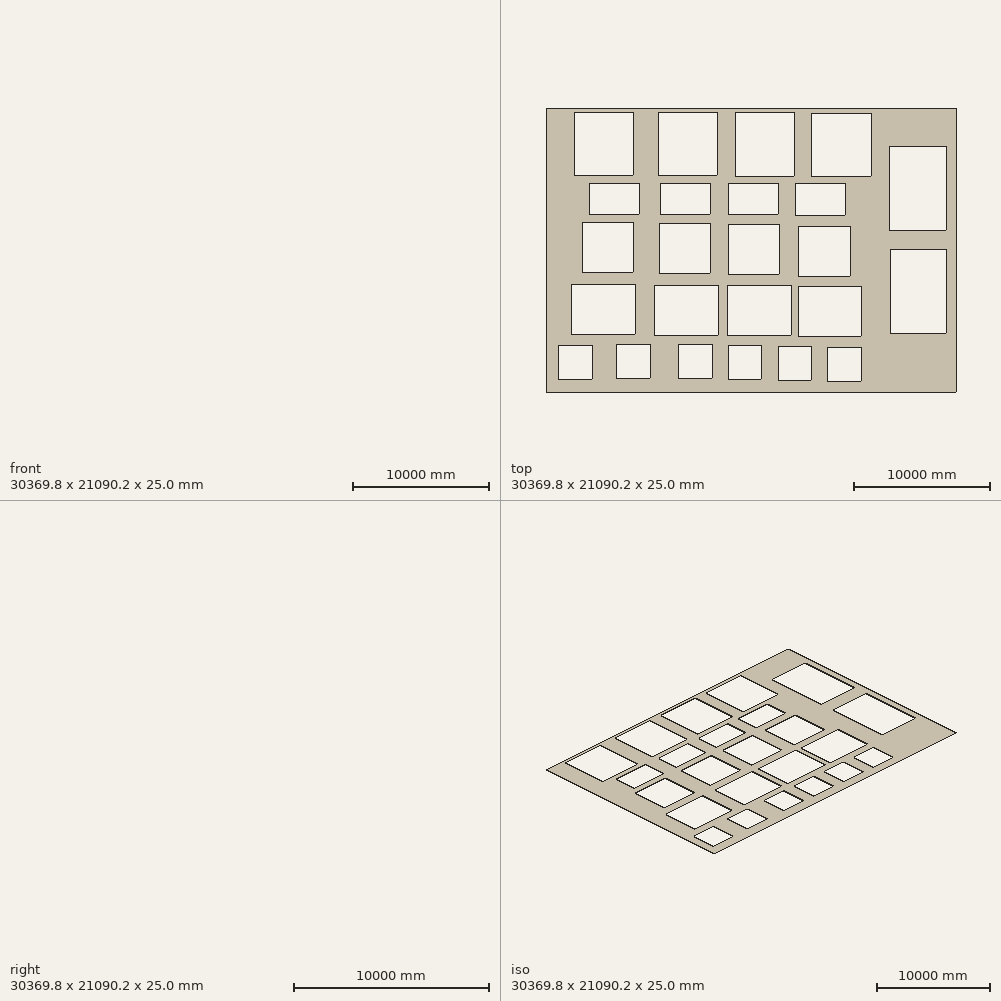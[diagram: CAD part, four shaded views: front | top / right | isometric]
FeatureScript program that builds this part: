
annotation { "Feature Type Name" : "Feature", "Feature Type Description" : "" }
export const myFeature = defineFeature(function(context is Context, id is Id, definition is map)
    precondition{}
    {
        {
            var Q0;
            Q0=qCreatedBy(makeId("Top.planeOp"),FACE);
            var sketch = newSketch(context, id + "F0", { "sketchPlane" : qUnion([Q0])});
            skLineSegment(sketch, "E0.bottom", {"start": v(-362.28, 2339.56) * mm, "end": v(3337.72, 2339.56) * mm});
            skLineSegment(sketch, "E0.top", {"start": v(-362.28, 39.56) * mm, "end": v(3337.72, 39.56) * mm});
            skLineSegment(sketch, "E0.left", {"start": v(-362.28, 2339.56) * mm, "end": v(-362.28, 39.56) * mm});
            skLineSegment(sketch, "E0.right", {"start": v(3337.72, 2339.56) * mm, "end": v(3337.72, 39.56) * mm});
            skLineSegment(sketch, "E1.bottom", {"start": v(-5538.63, 7611.88) * mm, "end": v(-1138.63, 7611.88) * mm});
            skLineSegment(sketch, "E1.top", {"start": v(-5538.63, 2911.88) * mm, "end": v(-1138.63, 2911.88) * mm});
            skLineSegment(sketch, "E1.left", {"start": v(-5538.63, 7611.88) * mm, "end": v(-5538.63, 2911.88) * mm});
            skLineSegment(sketch, "E1.right", {"start": v(-1138.63, 7611.88) * mm, "end": v(-1138.63, 2911.88) * mm});
            skLineSegment(sketch, "E2.bottom", {"start": v(4609.45, 2304.21) * mm, "end": v(8309.45, 2304.21) * mm});
            skLineSegment(sketch, "E2.top", {"start": v(4609.45, 4.21) * mm, "end": v(8309.45, 4.21) * mm});
            skLineSegment(sketch, "E2.left", {"start": v(4609.45, 2304.21) * mm, "end": v(4609.45, 4.21) * mm});
            skLineSegment(sketch, "E2.right", {"start": v(8309.45, 2304.21) * mm, "end": v(8309.45, 4.21) * mm});
            skLineSegment(sketch, "E3.bottom", {"start": v(-10619.1, 2366.7) * mm, "end": v(-6919.1, 2366.7) * mm});
            skLineSegment(sketch, "E3.top", {"start": v(-10619.1, 66.7) * mm, "end": v(-6919.1, 66.7) * mm});
            skLineSegment(sketch, "E3.left", {"start": v(-10619.1, 2366.7) * mm, "end": v(-10619.1, 66.7) * mm});
            skLineSegment(sketch, "E3.right", {"start": v(-6919.1, 2366.7) * mm, "end": v(-6919.1, 66.7) * mm});
            skLineSegment(sketch, "E4.bottom", {"start": v(-11738.1, 7598.85) * mm, "end": v(-7338.1, 7598.85) * mm});
            skLineSegment(sketch, "E4.top", {"start": v(-11738.1, 2898.85) * mm, "end": v(-7338.1, 2898.85) * mm});
            skLineSegment(sketch, "E4.left", {"start": v(-11738.1, 7598.85) * mm, "end": v(-11738.1, 2898.85) * mm});
            skLineSegment(sketch, "E4.right", {"start": v(-7338.1, 7598.85) * mm, "end": v(-7338.1, 2898.85) * mm});
            skLineSegment(sketch, "E5.bottom", {"start": v(-5346.09, 2331.36) * mm, "end": v(-1646.09, 2331.36) * mm});
            skLineSegment(sketch, "E5.top", {"start": v(-5346.09, 31.36) * mm, "end": v(-1646.09, 31.36) * mm});
            skLineSegment(sketch, "E5.left", {"start": v(-5346.09, 2331.36) * mm, "end": v(-5346.09, 31.36) * mm});
            skLineSegment(sketch, "E5.right", {"start": v(-1646.09, 2331.36) * mm, "end": v(-1646.09, 31.36) * mm});
            skLineSegment(sketch, "E6.bottom", {"start": v(156.32, 7588.05) * mm, "end": v(4556.32, 7588.05) * mm});
            skLineSegment(sketch, "E6.top", {"start": v(156.32, 2888.05) * mm, "end": v(4556.32, 2888.05) * mm});
            skLineSegment(sketch, "E6.left", {"start": v(156.32, 7588.05) * mm, "end": v(156.32, 2888.05) * mm});
            skLineSegment(sketch, "E6.right", {"start": v(4556.32, 7588.05) * mm, "end": v(4556.32, 2888.05) * mm});
            skLineSegment(sketch, "E7.bottom", {"start": v(-11167.32, -569.05) * mm, "end": v(-7367.32, -569.05) * mm});
            skLineSegment(sketch, "E7.top", {"start": v(-11167.32, -4269.05) * mm, "end": v(-7367.32, -4269.05) * mm});
            skLineSegment(sketch, "E7.left", {"start": v(-11167.32, -569.05) * mm, "end": v(-11167.32, -4269.05) * mm});
            skLineSegment(sketch, "E7.right", {"start": v(-7367.32, -569.05) * mm, "end": v(-7367.32, -4269.05) * mm});
            skLineSegment(sketch, "E8.bottom", {"start": v(-5464.05, -630.23) * mm, "end": v(-1664.05, -630.23) * mm});
            skLineSegment(sketch, "E8.top", {"start": v(-5464.05, -4330.23) * mm, "end": v(-1664.05, -4330.23) * mm});
            skLineSegment(sketch, "E8.left", {"start": v(-5464.05, -630.23) * mm, "end": v(-5464.05, -4330.23) * mm});
            skLineSegment(sketch, "E8.right", {"start": v(-1664.05, -630.23) * mm, "end": v(-1664.05, -4330.23) * mm});
            skLineSegment(sketch, "E9.bottom", {"start": v(-363.23, -697.79) * mm, "end": v(3436.77, -697.79) * mm});
            skLineSegment(sketch, "E9.top", {"start": v(-363.23, -4397.79) * mm, "end": v(3436.77, -4397.79) * mm});
            skLineSegment(sketch, "E9.left", {"start": v(-363.23, -697.79) * mm, "end": v(-363.23, -4397.79) * mm});
            skLineSegment(sketch, "E9.right", {"start": v(3436.77, -697.79) * mm, "end": v(3436.77, -4397.79) * mm});
            skLineSegment(sketch, "E10.bottom", {"start": v(4872.71, -832.91) * mm, "end": v(8672.71, -832.91) * mm});
            skLineSegment(sketch, "E10.top", {"start": v(4872.71, -4532.91) * mm, "end": v(8672.71, -4532.91) * mm});
            skLineSegment(sketch, "E10.left", {"start": v(4872.71, -832.91) * mm, "end": v(4872.71, -4532.91) * mm});
            skLineSegment(sketch, "E10.right", {"start": v(8672.71, -832.91) * mm, "end": v(8672.71, -4532.91) * mm});
            skLineSegment(sketch, "E11.bottom", {"start": v(5831.04, 7530.26) * mm, "end": v(10231.04, 7530.26) * mm});
            skLineSegment(sketch, "E11.top", {"start": v(5831.04, 2830.26) * mm, "end": v(10231.04, 2830.26) * mm});
            skLineSegment(sketch, "E11.left", {"start": v(5831.04, 7530.26) * mm, "end": v(5831.04, 2830.26) * mm});
            skLineSegment(sketch, "E11.right", {"start": v(10231.04, 7530.26) * mm, "end": v(10231.04, 2830.26) * mm});
            skLineSegment(sketch, "E12.bottom", {"start": v(-11939.89, -5119.18) * mm, "end": v(-7239.89, -5119.18) * mm});
            skLineSegment(sketch, "E12.top", {"start": v(-11939.89, -8819.18) * mm, "end": v(-7239.89, -8819.18) * mm});
            skLineSegment(sketch, "E12.left", {"start": v(-11939.89, -5119.18) * mm, "end": v(-11939.89, -8819.18) * mm});
            skLineSegment(sketch, "E12.right", {"start": v(-7239.89, -5119.18) * mm, "end": v(-7239.89, -8819.18) * mm});
            skLineSegment(sketch, "E13.bottom", {"start": v(-5802.73, -5186.74) * mm, "end": v(-1102.73, -5186.74) * mm});
            skLineSegment(sketch, "E13.top", {"start": v(-5802.73, -8886.74) * mm, "end": v(-1102.73, -8886.74) * mm});
            skLineSegment(sketch, "E13.left", {"start": v(-5802.73, -5186.74) * mm, "end": v(-5802.73, -8886.74) * mm});
            skLineSegment(sketch, "E13.right", {"start": v(-1102.73, -5186.74) * mm, "end": v(-1102.73, -8886.74) * mm});
            skLineSegment(sketch, "E14.bottom", {"start": v(-379.46, -5249.67) * mm, "end": v(4320.54, -5249.67) * mm});
            skLineSegment(sketch, "E14.top", {"start": v(-379.46, -8949.67) * mm, "end": v(4320.54, -8949.67) * mm});
            skLineSegment(sketch, "E14.left", {"start": v(-379.46, -5249.67) * mm, "end": v(-379.46, -8949.67) * mm});
            skLineSegment(sketch, "E14.right", {"start": v(4320.54, -5249.67) * mm, "end": v(4320.54, -8949.67) * mm});
            skLineSegment(sketch, "E15.bottom", {"start": v(4850, -5317.23) * mm, "end": v(9550, -5317.23) * mm});
            skLineSegment(sketch, "E15.top", {"start": v(4850, -9017.23) * mm, "end": v(9550, -9017.23) * mm});
            skLineSegment(sketch, "E15.left", {"start": v(4850, -5317.23) * mm, "end": v(4850, -9017.23) * mm});
            skLineSegment(sketch, "E15.right", {"start": v(9550, -5317.23) * mm, "end": v(9550, -9017.23) * mm});
            skLineSegment(sketch, "E16.bottom", {"start": v(-12920.44, -9653.54) * mm, "end": v(-10420.44, -9653.54) * mm});
            skLineSegment(sketch, "E16.top", {"start": v(-12920.44, -12153.54) * mm, "end": v(-10420.44, -12153.54) * mm});
            skLineSegment(sketch, "E16.left", {"start": v(-12920.44, -9653.54) * mm, "end": v(-12920.44, -12153.54) * mm});
            skLineSegment(sketch, "E16.right", {"start": v(-10420.44, -9653.54) * mm, "end": v(-10420.44, -12153.54) * mm});
            skLineSegment(sketch, "E17.bottom", {"start": v(-8596.7, -9586.1) * mm, "end": v(-6096.7, -9586.1) * mm});
            skLineSegment(sketch, "E17.top", {"start": v(-8596.7, -12086.1) * mm, "end": v(-6096.7, -12086.1) * mm});
            skLineSegment(sketch, "E17.left", {"start": v(-8596.7, -9586.1) * mm, "end": v(-8596.7, -12086.1) * mm});
            skLineSegment(sketch, "E17.right", {"start": v(-6096.7, -9586.1) * mm, "end": v(-6096.7, -12086.1) * mm});
            skLineSegment(sketch, "E18.bottom", {"start": v(-4036.36, -9586.1) * mm, "end": v(-1536.36, -9586.1) * mm});
            skLineSegment(sketch, "E18.top", {"start": v(-4036.36, -12086.1) * mm, "end": v(-1536.36, -12086.1) * mm});
            skLineSegment(sketch, "E18.left", {"start": v(-4036.36, -9586.1) * mm, "end": v(-4036.36, -12086.1) * mm});
            skLineSegment(sketch, "E18.right", {"start": v(-1536.36, -9586.1) * mm, "end": v(-1536.36, -12086.1) * mm});
            skLineSegment(sketch, "E19.bottom", {"start": v(-354.31, -9653.67) * mm, "end": v(2145.69, -9653.67) * mm});
            skLineSegment(sketch, "E19.top", {"start": v(-354.31, -12153.67) * mm, "end": v(2145.69, -12153.67) * mm});
            skLineSegment(sketch, "E19.left", {"start": v(-354.31, -9653.67) * mm, "end": v(-354.31, -12153.67) * mm});
            skLineSegment(sketch, "E19.right", {"start": v(2145.69, -9653.67) * mm, "end": v(2145.69, -12153.67) * mm});
            skLineSegment(sketch, "E20.bottom", {"start": v(3344.63, -9721.23) * mm, "end": v(5844.63, -9721.23) * mm});
            skLineSegment(sketch, "E20.top", {"start": v(3344.63, -12221.23) * mm, "end": v(5844.63, -12221.23) * mm});
            skLineSegment(sketch, "E20.left", {"start": v(3344.63, -9721.23) * mm, "end": v(3344.63, -12221.23) * mm});
            skLineSegment(sketch, "E20.right", {"start": v(5844.63, -9721.23) * mm, "end": v(5844.63, -12221.23) * mm});
            skLineSegment(sketch, "E21.bottom", {"start": v(7026.67, -9788.79) * mm, "end": v(9526.67, -9788.79) * mm});
            skLineSegment(sketch, "E21.top", {"start": v(7026.67, -12288.79) * mm, "end": v(9526.67, -12288.79) * mm});
            skLineSegment(sketch, "E21.left", {"start": v(7026.67, -9788.79) * mm, "end": v(7026.67, -12288.79) * mm});
            skLineSegment(sketch, "E21.right", {"start": v(9526.67, -9788.79) * mm, "end": v(9526.67, -12288.79) * mm});
            skLineSegment(sketch, "E22.bottom", {"start": v(11638.82, -2548.27) * mm, "end": v(15838.82, -2548.27) * mm});
            skLineSegment(sketch, "E22.top", {"start": v(11638.82, -8798.27) * mm, "end": v(15838.82, -8798.27) * mm});
            skLineSegment(sketch, "E22.left", {"start": v(11638.82, -2548.27) * mm, "end": v(11638.82, -8798.27) * mm});
            skLineSegment(sketch, "E22.right", {"start": v(15838.82, -2548.27) * mm, "end": v(15838.82, -8798.27) * mm});
            skLineSegment(sketch, "E23.bottom", {"start": v(11627.75, 5092.75) * mm, "end": v(15827.75, 5092.75) * mm});
            skLineSegment(sketch, "E23.top", {"start": v(11627.75, -1157.25) * mm, "end": v(15827.75, -1157.25) * mm});
            skLineSegment(sketch, "E23.left", {"start": v(11627.75, 5092.75) * mm, "end": v(11627.75, -1157.25) * mm});
            skLineSegment(sketch, "E23.right", {"start": v(15827.75, 5092.75) * mm, "end": v(15827.75, -1157.25) * mm});
            skLineSegment(sketch, "E24.bottom", {"start": v(-13810.57, 7923.12) * mm, "end": v(16559.27, 7923.12) * mm});
            skLineSegment(sketch, "E24.top", {"start": v(-13810.57, -13167.04) * mm, "end": v(16559.27, -13167.04) * mm});
            skLineSegment(sketch, "E24.left", {"start": v(-13810.57, 7923.12) * mm, "end": v(-13810.57, -13167.04) * mm});
            skLineSegment(sketch, "E24.right", {"start": v(16559.27, 7923.12) * mm, "end": v(16559.27, -13167.04) * mm});
            skSolve(sketch);
        }
        {
            var Q0;
            Q0 = qSketchRegion(id + "F0", true);
            extrude(context, id + "F1", {"entities" : qUnion([Q0]), "depth" : 25 * mm, "offsetDistance" : 25 * mm});
        }
    });
